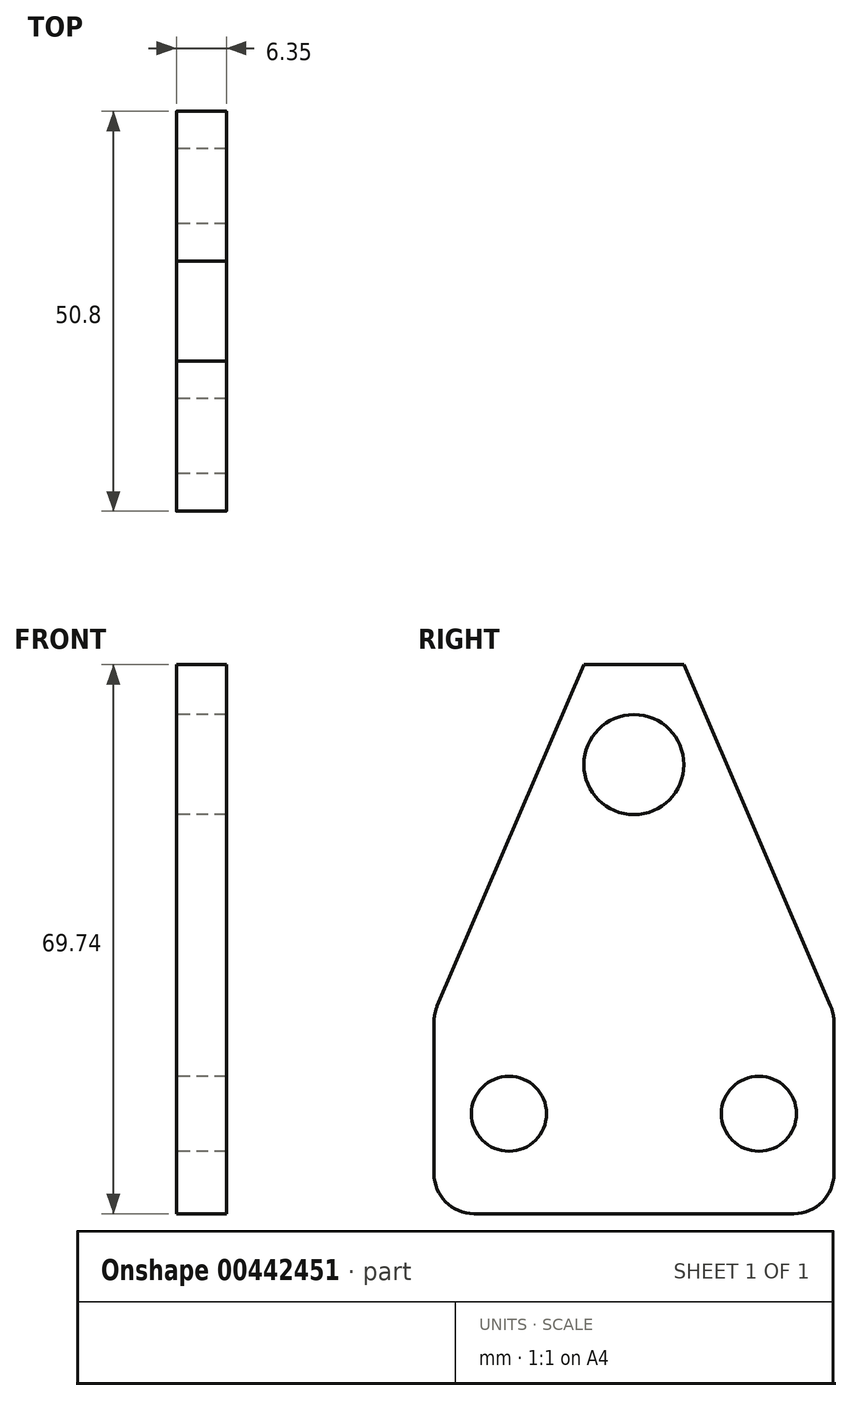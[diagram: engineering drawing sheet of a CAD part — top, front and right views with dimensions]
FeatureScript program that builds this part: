
annotation { "Feature Type Name" : "Feature", "Feature Type Description" : "" }
export const myFeature = defineFeature(function(context is Context, id is Id, definition is map)
    precondition{}
    {
        {
            var Q0;
            Q0=qCreatedBy(makeId("Right.planeOp"),FACE);
            var sketch = newSketch(context, id + "F0", { "sketchPlane" : qUnion([Q0])});
            skLineSegment(sketch, "E0.bottom", {"start": v(25.4, 12.7) * mm, "end": v(-25.4, 12.7) * mm});
            skLineSegment(sketch, "E0.top", {"start": v(25.4, -12.7) * mm, "end": v(-25.4, -12.7) * mm});
            skLineSegment(sketch, "E0.left", {"start": v(25.4, 12.7) * mm, "end": v(25.4, -12.7) * mm});
            skLineSegment(sketch, "E0.right", {"start": v(-25.4, 12.7) * mm, "end": v(-25.4, -12.7) * mm});
            skPoint(sketch, "E0.middle", {"position": v(0, 0) * mm});
            skCircle(sketch, "E1", {"center": v(0, 44.34) * mm, "radius": 6.35 * mm});
            skCircle(sketch, "E2", {"center": v(15.88, 0) * mm, "radius": 4.76 * mm});
            skCircle(sketch, "E3", {"center": v(-15.88, 0) * mm, "radius": 4.76 * mm});
            skLineSegment(sketch, "E4", {"start": v(-25.4, 12.7) * mm, "end": v(-6.35, 57.04) * mm});
            skLineSegment(sketch, "E5", {"start": v(25.4, 12.7) * mm, "end": v(6.35, 57.04) * mm});
            skLineSegment(sketch, "E6", {"start": v(6.35, 57.04) * mm, "end": v(-6.35, 57.04) * mm});
            skSolve(sketch);
        }
        {
            var Q0;
            Q0 = qSketchRegion(id + "F0", true);
            extrude(context, id + "F1", {"entities" : qUnion([Q0]), "depth" : 6.35 * mm});
        }
        {
            var Q0;
            Q0=makeQuery(id+"F1.opExtrude","SWEPT_EDGE",EDGE,{"disambiguationData":[OSD([sQuery(id+"F0.wireOp",EDGE,"E0.top"),sQuery(id+"F0.wireOp",EDGE,"E0.right")])]});
            var Q1;
            Q1=makeQuery(id+"F1.opExtrude","SWEPT_EDGE",EDGE,{"disambiguationData":[OSD([sQuery(id+"F0.wireOp",EDGE,"E0.top"),sQuery(id+"F0.wireOp",EDGE,"E0.left")])]});
            var Q2;
            Q2=makeQuery(id+"F1.opExtrude","SWEPT_EDGE",EDGE,{"disambiguationData":[OSD([sQuery(id+"F0.wireOp",EDGE,"E0.bottom"),sQuery(id+"F0.wireOp",EDGE,"E0.left"),sQuery(id+"F0.wireOp",EDGE,"816cfad8-fb1a-4ff9-8639-9da4710b3a50")])]});
            var Q3;
            Q3=makeQuery(id+"F1.opExtrude","SWEPT_EDGE",EDGE,{"disambiguationData":[OSD([sQuery(id+"F0.wireOp",EDGE,"E0.bottom"),sQuery(id+"F0.wireOp",EDGE,"E0.right"),sQuery(id+"F0.wireOp",EDGE,"816cfad8-fb1a-4ff9-8639-9da4710b3a50")])]});
            fillet(context, id + "F2", {"entities" : qUnion([Q0, Q1, Q2, Q3]), "radius" : 5.08 * mm, "tangentPropagation" : true, "allowEdgeOverflow" : false});
        }
    });
